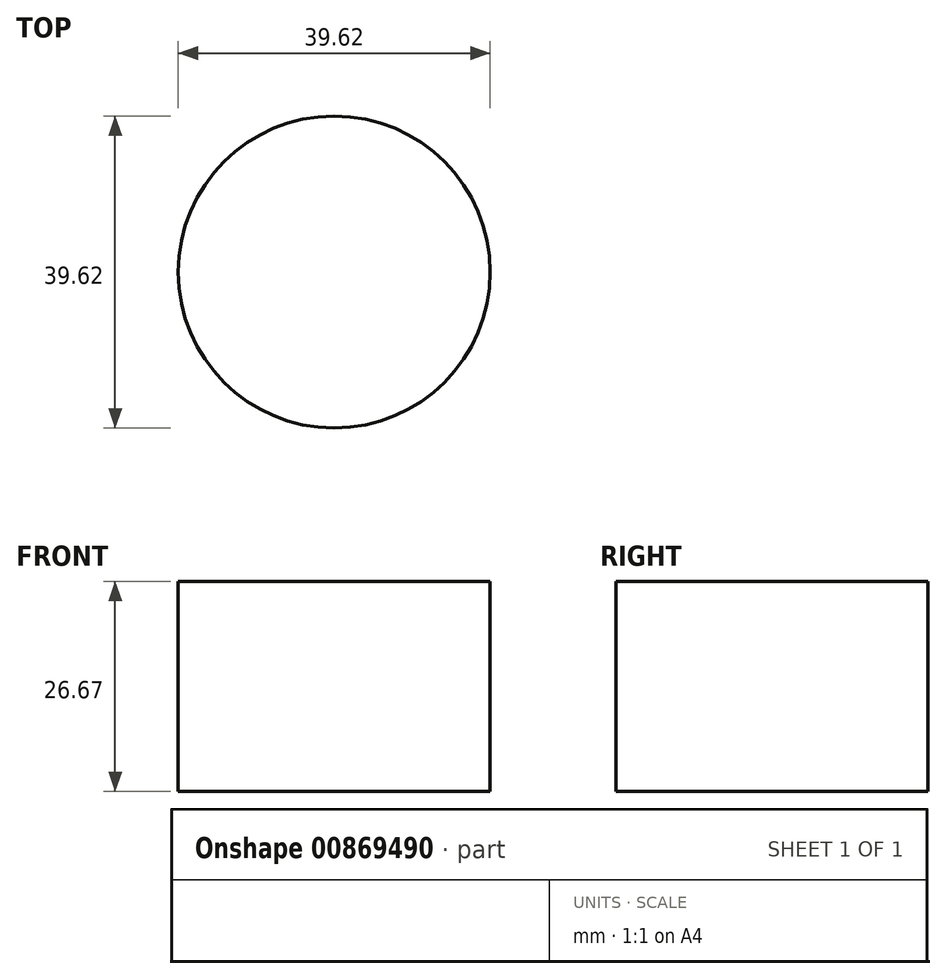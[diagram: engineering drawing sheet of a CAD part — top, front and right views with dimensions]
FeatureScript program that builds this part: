
annotation { "Feature Type Name" : "Feature", "Feature Type Description" : "" }
export const myFeature = defineFeature(function(context is Context, id is Id, definition is map)
    precondition{}
    {
        {
            var Q0;
            Q0=qCreatedBy(makeId("Top.planeOp"),FACE);
            var sketch = newSketch(context, id + "F0", { "sketchPlane" : qUnion([Q0])});
            skCircle(sketch, "E0", {"center": v(0, 0) * mm, "radius": 19.81 * mm});
            skSolve(sketch);
        }
        {
            var Q0;
            Q0 = qSketchRegion(id + "F0", true);
            extrude(context, id + "F1", {"entities" : qUnion([Q0]), "depth" : 26.67 * mm, "offsetDistance" : 25.4 * mm});
        }
    });
